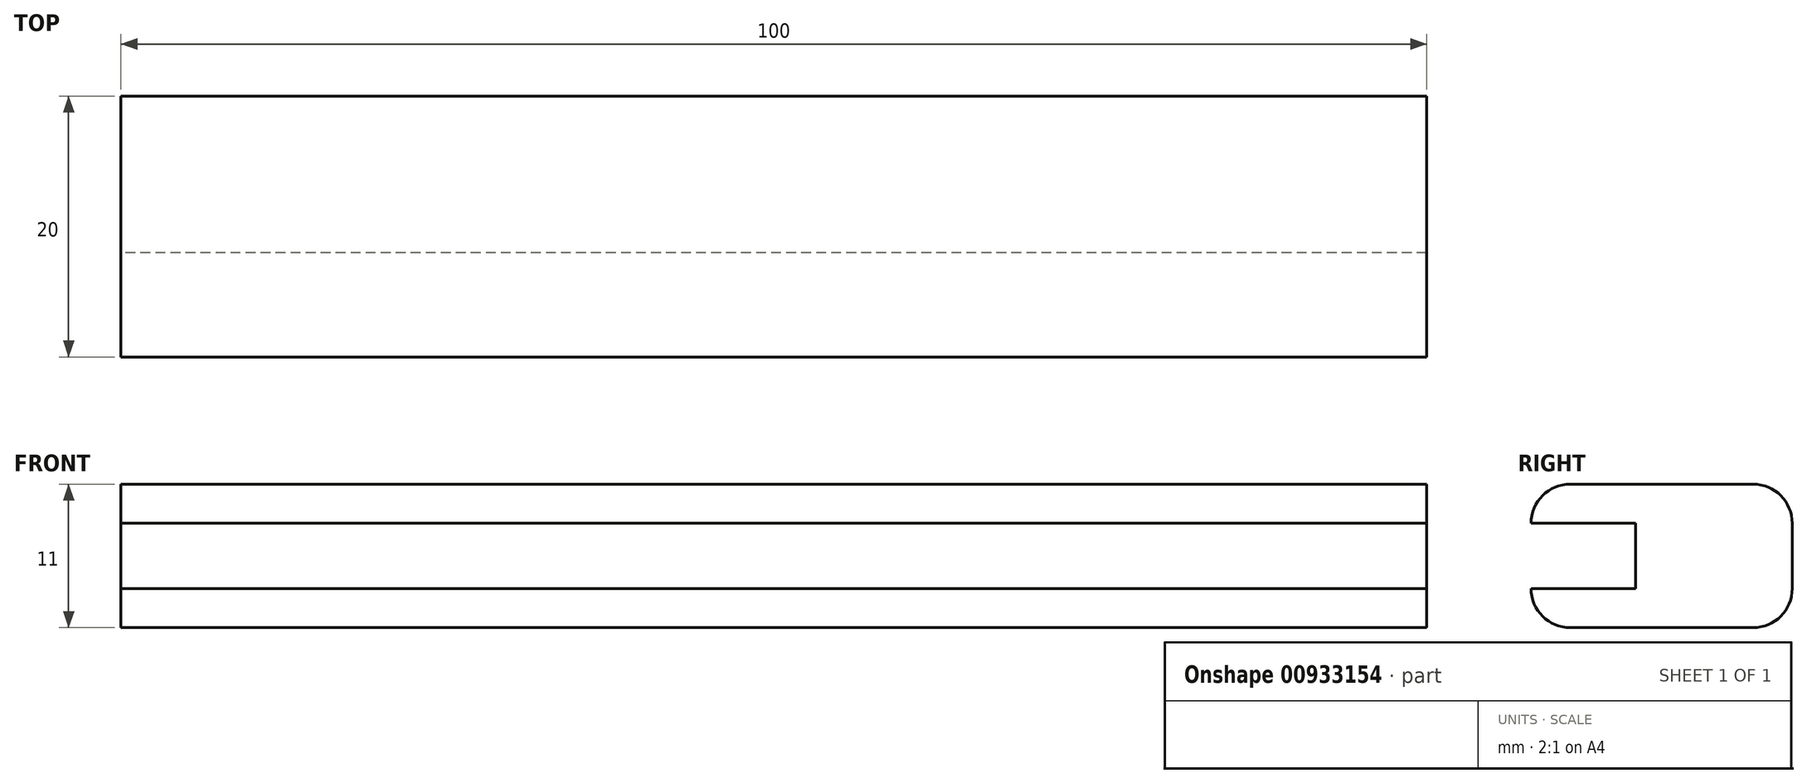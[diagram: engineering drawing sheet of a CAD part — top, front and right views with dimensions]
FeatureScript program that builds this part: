
annotation { "Feature Type Name" : "Feature", "Feature Type Description" : "" }
export const myFeature = defineFeature(function(context is Context, id is Id, definition is map)
    precondition{}
    {
        {
            var Q0;
            Q0=qCreatedBy(makeId("Front.planeOp"),FACE);
            var sketch = newSketch(context, id + "F0", { "sketchPlane" : qUnion([Q0])});
            skLineSegment(sketch, "E0.bottom", {"start": v(-50, -5.5) * mm, "end": v(50, -5.5) * mm});
            skLineSegment(sketch, "E0.top", {"start": v(-50, 5.5) * mm, "end": v(50, 5.5) * mm});
            skLineSegment(sketch, "E0.left", {"start": v(-50, -5.5) * mm, "end": v(-50, 5.5) * mm});
            skLineSegment(sketch, "E0.right", {"start": v(50, -5.5) * mm, "end": v(50, 5.5) * mm});
            skPoint(sketch, "E0.middle", {"position": v(0, 0) * mm});
            skSolve(sketch);
        }
        {
            var Q0;
            Q0=makeQuery(id+"F0.imprint","IMPRINT",FACE,{"disambiguationData":[TD([[makeQuery(id+"F0.imprint","IMPRINT",EDGE,{"derivedFrom":sQuery(id+"F0.wireOp",EDGE,"E0.bottom")}),1.0]])]});
            extrude(context, id + "F1", {"entities" : qUnion([Q0]), "oppositeDirection" : true, "depth" : 20 * mm, "offsetDistance" : 25 * mm});
        }
        {
            var Q0;
            Q0=makeQuery(id+"F1.opExtrude","CAP_FACE",FACE,{"disambiguationData":[OSD([sQuery(id+"F0.wireOp",EDGE,"E0.bottom"),sQuery(id+"F0.wireOp",EDGE,"E0.top"),sQuery(id+"F0.wireOp",EDGE,"E0.left"),sQuery(id+"F0.wireOp",EDGE,"E0.right")])],"isStart":true});
            var sketch = newSketch(context, id + "F2", { "sketchPlane" : qUnion([Q0])});
            skLineSegment(sketch, "E1.bottom", {"start": v(50, -2.5) * mm, "end": v(-50, -2.5) * mm});
            skLineSegment(sketch, "E1.top", {"start": v(50, 2.5) * mm, "end": v(-50, 2.5) * mm});
            skLineSegment(sketch, "E1.left", {"start": v(50, -2.5) * mm, "end": v(50, 2.5) * mm});
            skLineSegment(sketch, "E1.right", {"start": v(-50, -2.5) * mm, "end": v(-50, 2.5) * mm});
            skPoint(sketch, "E1.middle", {"position": v(0, 0) * mm});
            skSolve(sketch);
        }
        {
            var Q0;
            Q0=makeQuery(id+"F2.imprint","IMPRINT",FACE,{"disambiguationData":[TD([[makeQuery(id+"F2.imprint","IMPRINT",EDGE,{"derivedFrom":sQuery(id+"F2.wireOp",EDGE,"E1.bottom")}),-1.0]])]});
            extrude(context, id + "F3", {"entities" : qUnion([Q0]), "operationType" : NewBodyOperationType.REMOVE, "oppositeDirection" : true, "depth" : 8 * mm, "offsetDistance" : 25 * mm});
        }
        {
            var Q0;
            Q0=makeQuery(id+"F1.opExtrude","CAP_EDGE",EDGE,{"disambiguationData":[OSD([sQuery(id+"F0.wireOp",EDGE,"E0.top")])],"isStart":false});
            var Q1;
            Q1=makeQuery(id+"F1.opExtrude","CAP_EDGE",EDGE,{"disambiguationData":[OSD([sQuery(id+"F0.wireOp",EDGE,"E0.bottom")])],"isStart":false});
            var Q2;
            Q2=makeQuery(id+"F1.opExtrude","CAP_EDGE",EDGE,{"disambiguationData":[OSD([sQuery(id+"F0.wireOp",EDGE,"E0.top")])],"isStart":true});
            var Q3;
            Q3=makeQuery(id+"F1.opExtrude","CAP_EDGE",EDGE,{"disambiguationData":[OSD([sQuery(id+"F0.wireOp",EDGE,"E0.bottom")])],"isStart":true});
            fillet(context, id + "F4", {"entities" : qUnion([Q0, Q1, Q2, Q3]), "radius" : 3 * mm, "tangentPropagation" : true, "allowEdgeOverflow" : false});
        }
    });
